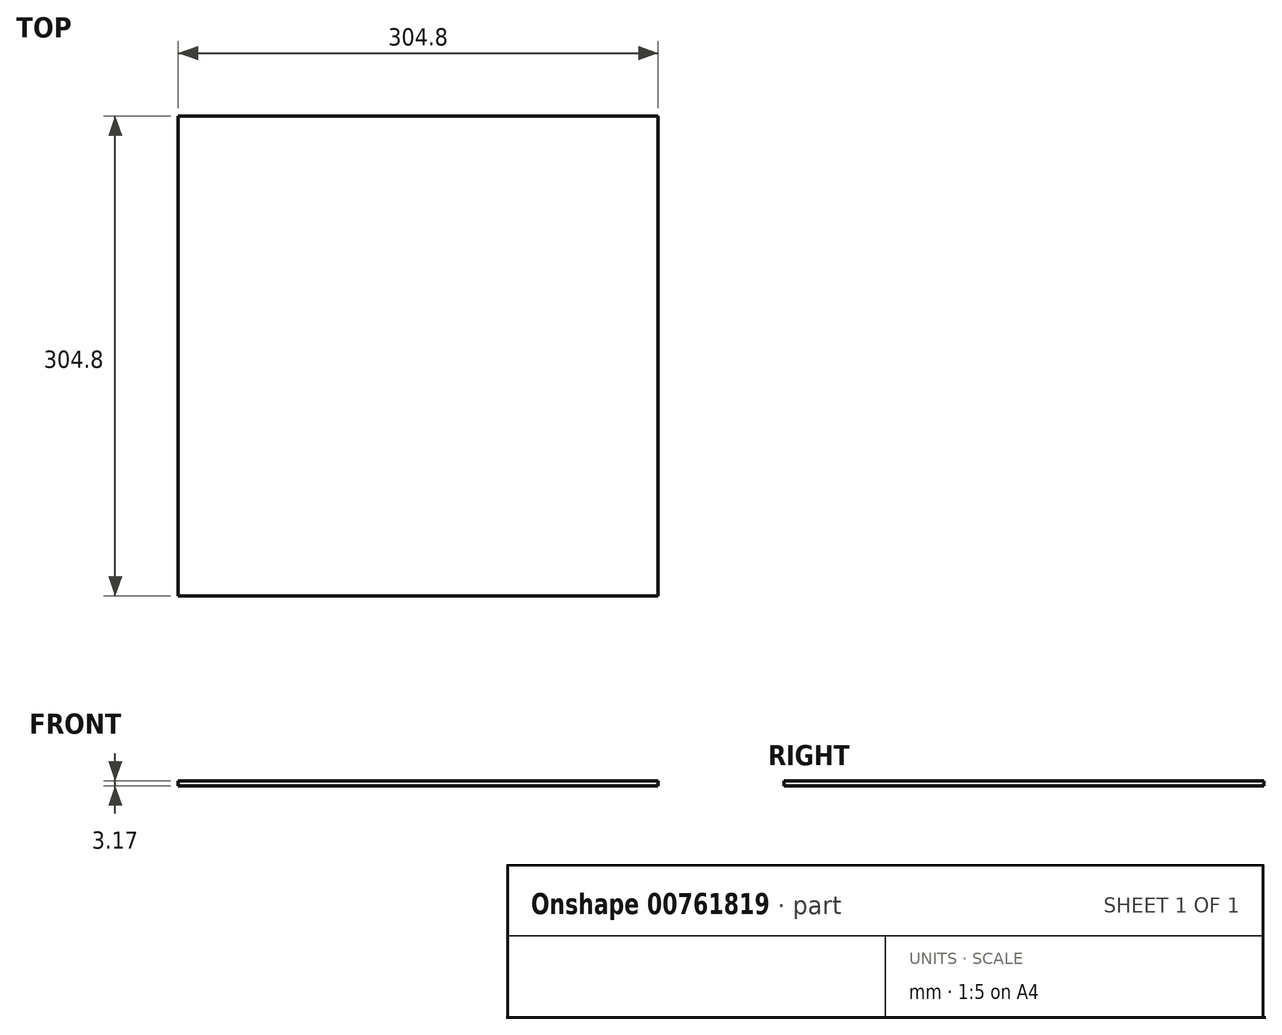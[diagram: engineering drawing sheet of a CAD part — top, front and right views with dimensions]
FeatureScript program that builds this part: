
annotation { "Feature Type Name" : "Feature", "Feature Type Description" : "" }
export const myFeature = defineFeature(function(context is Context, id is Id, definition is map)
    precondition{}
    {
        {
            var Q0;
            Q0=qCreatedBy(makeId("Top.planeOp"),FACE);
            var sketch = newSketch(context, id + "F0", { "sketchPlane" : qUnion([Q0])});
            skLineSegment(sketch, "E0.bottom", {"start": v(184.87, -172.37) * mm, "end": v(-119.93, -172.37) * mm});
            skLineSegment(sketch, "E0.top", {"start": v(184.87, 132.43) * mm, "end": v(-119.93, 132.43) * mm});
            skLineSegment(sketch, "E0.left", {"start": v(184.87, -172.37) * mm, "end": v(184.87, 132.43) * mm});
            skLineSegment(sketch, "E0.right", {"start": v(-119.93, -172.37) * mm, "end": v(-119.93, 132.43) * mm});
            skSolve(sketch);
        }
        {
            var Q0;
            Q0 = qSketchRegion(id + "F0", true);
            extrude(context, id + "F1", {"entities" : qUnion([Q0]), "depth" : 3.17 * mm, "offsetDistance" : 25.4 * mm});
        }
    });
